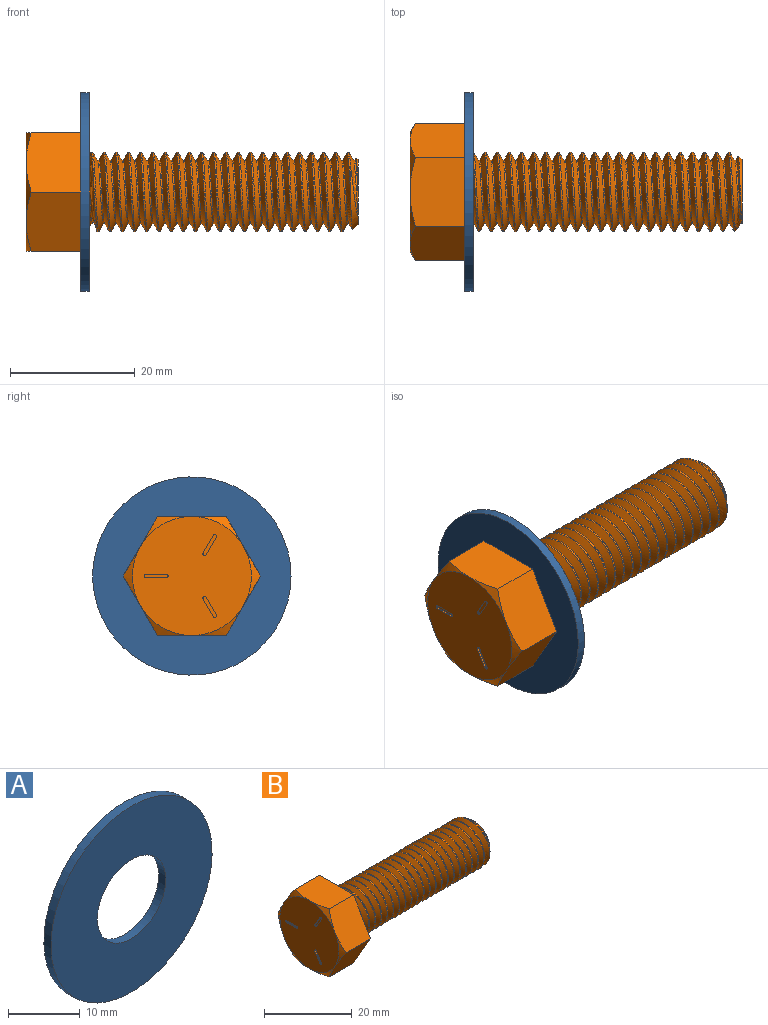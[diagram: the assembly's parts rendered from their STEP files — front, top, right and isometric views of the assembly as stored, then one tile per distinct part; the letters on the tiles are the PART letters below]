
ASSEMBLY  parts=2 mates=1
PART A: 4 faces, bbox 31.8x1.4x31.8 mm
  f0: cylinder r=15.88mm len=31.75mm, axis (0,-1,0), area 139.3mm2, adj f1,f2
  f1: plane 31.75x31.75mm, normal (0,1,0), area 648.9mm2, adj f0,f3
  f2: plane 31.75x31.75mm, normal (0,-1,0), area 648.9mm2, adj f0,f3
  f3: cylinder r=6.74mm len=13.49mm, axis (0,1,0), area 59.2mm2, adj f1,f2
PART B: 35 faces, bbox 55x22.9x22.9 mm
  f0: plane 11.91x9.64mm, normal (0,0,1), area 92.8mm2, adj f1,f5,f12,f13,f18
  f1: plane 10.43x9.64mm, normal (0,0.87,0.5), area 92.8mm2, adj f0,f2,f12,f17,f18
  f2: plane 10.43x9.64mm, normal (0,0.87,-0.5), area 92.8mm2, adj f1,f3,f12,f16,f17
  f3: plane 11.91x9.64mm, normal (0,0,-1), area 92.8mm2, adj f2,f4,f12,f15,f16
  f4: plane 10.43x9.64mm, normal (0,-0.87,-0.5), area 92.8mm2, adj f3,f5,f12,f14,f15
  f5: plane 10.43x9.64mm, normal (0,-0.87,0.5), area 92.8mm2, adj f0,f4,f12,f13,f14
  f6: cylinder r=6.35mm len=43.25mm, axis (1,0,0), area 284.6mm2, adj f8,f10,f11,f12
  f7: plane 10.32x10.28mm, normal (1,0,0), area 83.1mm2, adj f8,f9,f10,f11
  f8: cone r=5.15mm half-angle=45deg, axis (-1,0,0), area 28.5mm2, adj f6,f7,f10,f11
  f9: bspline ~45.18x10.69mm, area 177.4mm2, adj f7,f10,f11,f12
  f10: bspline ~45.48x13.35mm, area 1182.4mm2, adj f6,f7,f8,f9,f12
  f11: bspline ~46.26x13.35mm, area 1183.5mm2, adj f6,f7,f8,f9,f12
  f12: plane 22.01x19.07mm, normal (1,0,0), area 211mm2, adj f0,f1,f2,f3,f4,f5,f6,f9
  f13: cone r=9.53mm half-angle=60deg, axis (1,0,0), area 8.9mm2, adj f0,f5,f19
  f14: cone r=9.53mm half-angle=60deg, axis (1,0,0), area 8.9mm2, adj f4,f5,f19
  f15: cone r=9.53mm half-angle=60deg, axis (1,0,0), area 8.9mm2, adj f3,f4,f19
  f16: cone r=9.53mm half-angle=60deg, axis (1,0,0), area 8.9mm2, adj f2,f3,f19
  f17: cone r=9.53mm half-angle=60deg, axis (1,0,0), area 8.9mm2, adj f1,f2,f19
  f18: cone r=9.53mm half-angle=60deg, axis (1,0,0), area 8.9mm2, adj f0,f1,f19
  f19: plane 19.05x19.05mm, normal (-1,0,0), area 278.7mm2, adj f13,f14,f15,f16,f17,f18,f20,f21
  f20: cylinder r=0.29mm len=0.57mm, axis (-1,0,0), area 0.2mm2, adj f19,f21,f23,f24
  f21: plane 3.24x0.25mm, normal (0,0,-1), area 0.8mm2, adj f19,f20,f22,f24
  f22: cylinder r=0.29mm len=0.57mm, axis (-1,0,0), area 0.2mm2, adj f19,f21,f23,f24
  f23: plane 3.24x0.25mm, normal (0,0,1), area 0.8mm2, adj f19,f20,f22,f24
  f24: plane 3.81x0.57mm, normal (-1,0,0), area 2.1mm2, adj f20,f21,f22,f23
  f25: cylinder r=0.29mm len=0.53mm, axis (-1,0,0), area 0.2mm2, adj f19,f26,f28,f29
  f26: plane 2.8x1.62mm, normal (0,0.87,0.5), area 0.8mm2, adj f19,f25,f27,f29
  f27: cylinder r=0.29mm len=0.53mm, axis (-1,0,0), area 0.2mm2, adj f19,f26,f28,f29
  f28: plane 2.8x1.62mm, normal (0,-0.87,-0.5), area 0.8mm2, adj f19,f25,f27,f29
  f29: plane 3.38x2.19mm, normal (-1,0,0), area 2.1mm2, adj f25,f26,f27,f28
  f30: cylinder r=0.29mm len=0.53mm, axis (-1,0,0), area 0.2mm2, adj f19,f31,f33,f34
  f31: plane 2.8x1.62mm, normal (0,-0.87,0.5), area 0.8mm2, adj f19,f30,f32,f34
  f32: cylinder r=0.29mm len=0.53mm, axis (-1,0,0), area 0.2mm2, adj f19,f31,f33,f34
  f33: plane 2.8x1.62mm, normal (0,0.87,-0.5), area 0.8mm2, adj f19,f30,f32,f34
  f34: plane 3.38x2.19mm, normal (-1,0,0), area 2.1mm2, adj f30,f31,f32,f33
PLACE A rot(axis=(0.58,0.58,-0.58),120deg) t=(-13.24,2.5,-0.25)mm
PLACE B t=(4.61,2.5,-0.25)mm fixed
MATE fastened A.f0 <-> B.f6  axis (-1,0,0) through (-13.24,2.5,-0.25)mm
